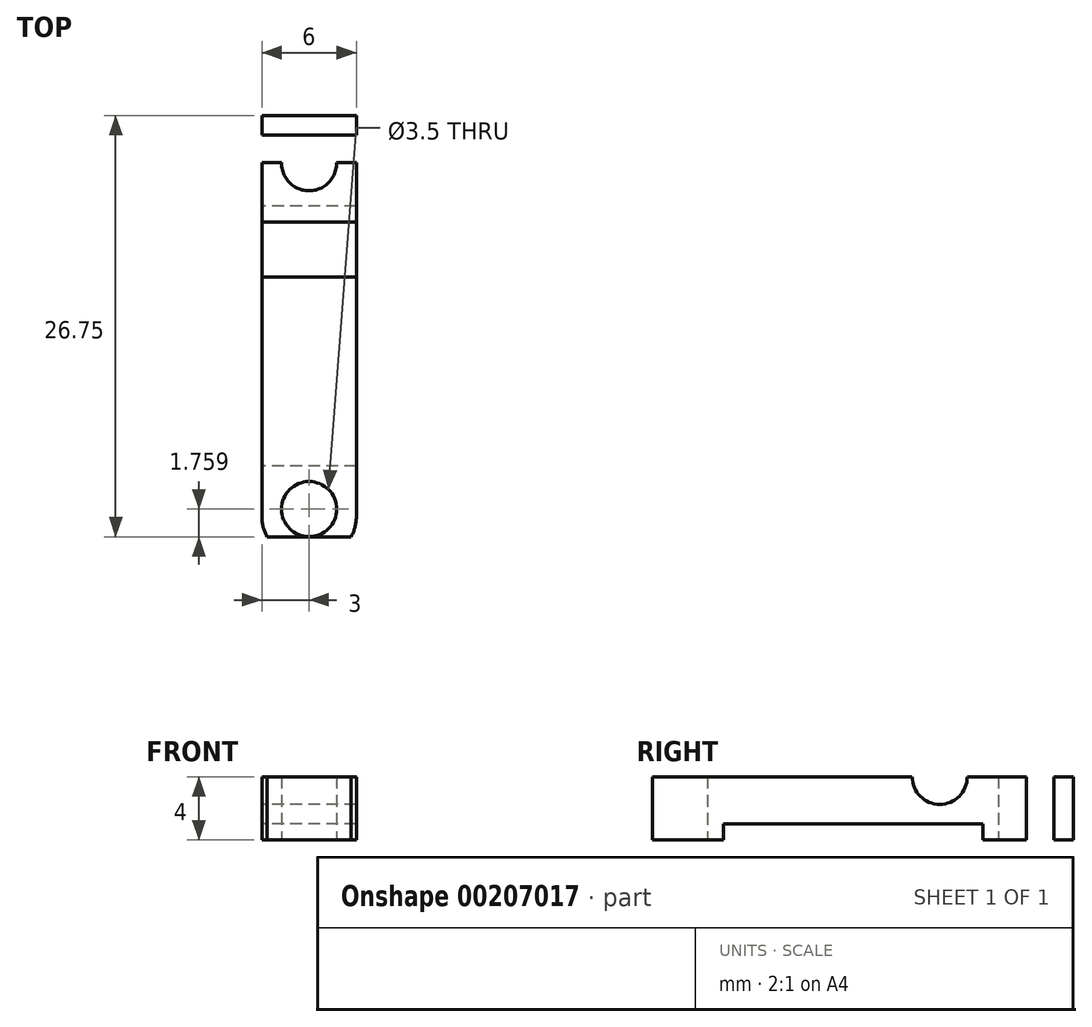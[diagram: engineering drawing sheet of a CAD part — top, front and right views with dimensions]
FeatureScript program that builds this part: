
annotation { "Feature Type Name" : "Feature", "Feature Type Description" : "" }
export const myFeature = defineFeature(function(context is Context, id is Id, definition is map)
    precondition{}
    {
        {
            var Q0;
            Q0=qCreatedBy(makeId("Right.planeOp"),FACE);
            var sketch = newSketch(context, id + "F0", { "sketchPlane" : qUnion([Q0])});
            skLineSegment(sketch, "E0.bottom", {"start": v(-33.45, -2.24) * mm, "end": v(-38.2, -2.24) * mm});
            skLineSegment(sketch, "E0.top", {"start": v(-33.45, 1.76) * mm, "end": v(-41.95, 1.76) * mm});
            skLineSegment(sketch, "E0.left", {"start": v(-33.45, -2.24) * mm, "end": v(-33.45, 1.76) * mm});
            skLineSegment(sketch, "E0.right", {"start": v(-61.45, -2.24) * mm, "end": v(-61.45, 1.76) * mm});
            skPoint(sketch, "E0.middle", {"position": v(-47.45, -0.24) * mm});
            skLineSegment(sketch, "E1", {"start": v(-61.45, -2.24) * mm, "end": v(-58.45, -2.24) * mm});
            skLineSegment(sketch, "E2", {"start": v(-58.45, 1.76) * mm, "end": v(-58.45, -2.24) * mm});
            skLineSegment(sketch, "E3", {"start": v(-33.45, -2.24) * mm, "end": v(-36.45, -2.24) * mm});
            skLineSegment(sketch, "E4", {"start": v(-36.45, -2.24) * mm, "end": v(-36.45, 1.76) * mm});
            skLineSegment(sketch, "E5", {"start": v(-61.45, 1.76) * mm, "end": v(-42.45, 1.76) * mm});
            skLineSegment(sketch, "E6", {"start": v(-33.45, 1.76) * mm, "end": v(-41.45, 1.76) * mm});
            skCircle(sketch, "E7", {"center": v(-41.95, 1.76) * mm, "radius": 1.75 * mm});
            skLineSegment(sketch, "E8", {"start": v(-36.45, 1.76) * mm, "end": v(-38.2, 1.76) * mm});
            skLineSegment(sketch, "E9", {"start": v(-38.2, 1.76) * mm, "end": v(-34.7, 1.76) * mm});
            skLineSegment(sketch, "E10", {"start": v(-58.45, 1.76) * mm, "end": v(-56.7, 1.76) * mm});
            skLineSegment(sketch, "E11", {"start": v(-56.7, 1.76) * mm, "end": v(-60.2, 1.76) * mm});
            skLineSegment(sketch, "E12", {"start": v(-60.2, 1.76) * mm, "end": v(-61.45, 1.76) * mm});
            skLineSegment(sketch, "E13", {"start": v(-58.45, -2.24) * mm, "end": v(-56.7, -2.24) * mm});
            skLineSegment(sketch, "E14", {"start": v(-56.7, 1.76) * mm, "end": v(-56.7, -2.24) * mm});
            skLineSegment(sketch, "E15", {"start": v(-56.7, -2.24) * mm, "end": v(-56.7, -1.49) * mm});
            skPoint(sketch, "E16.visualSharp", {"position": v(-56.7, -1.24) * mm});
            skPoint(sketch, "E17.visualSharp", {"position": v(-38.2, -1.24) * mm});
            skLineSegment(sketch, "E18", {"start": v(-61.45, -0.24) * mm, "end": v(-61.45, 1.76) * mm});
            skLineSegment(sketch, "E19", {"start": v(-61.45, -0.24) * mm, "end": v(-61.45, -2.24) * mm});
            skLineSegment(sketch, "E20", {"start": v(-60.2, 1.76) * mm, "end": v(-60.2, -2.24) * mm});
            skLineSegment(sketch, "E21.trimOffspring", {"start": v(-38.2, -2.24) * mm, "end": v(-36.45, -2.24) * mm});
            skLineSegment(sketch, "E22.trimOffspring", {"start": v(-56.7, -2.24) * mm, "end": v(-61.45, -2.24) * mm});
            skLineSegment(sketch, "E23.trimOffspring", {"start": v(-42.45, 1.76) * mm, "end": v(-61.45, 1.76) * mm});
            skLineSegment(sketch, "E24", {"start": v(-34.7, 1.76) * mm, "end": v(-34.7, -2.24) * mm});
            skLineSegment(sketch, "E25", {"start": v(-34.7, -2.24) * mm, "end": v(-33.45, -2.24) * mm});
            skLineSegment(sketch, "E26", {"start": v(-56.7, -2.24) * mm, "end": v(-55.7, -2.24) * mm});
            skLineSegment(sketch, "E27", {"start": v(-55.7, -1.24) * mm, "end": v(-55.7, -2.24) * mm});
            skLineSegment(sketch, "E28", {"start": v(-38.2, -2.24) * mm, "end": v(-39.2, -2.24) * mm});
            skLineSegment(sketch, "E29", {"start": v(-39.2, -1.24) * mm, "end": v(-39.2, -2.24) * mm});
            skLineSegment(sketch, "E30", {"start": v(-55.7, -1.24) * mm, "end": v(-39.2, -1.24) * mm});
            skCircle(sketch, "E31", {"center": v(-41.95, 1.76) * mm, "radius": 0.75 * mm});
            skSolve(sketch);
        }
        {
            var Q0;
            {var subQ0=sQuery(id+"F0.wireOp",EDGE,"E2");Q0=makeQuery(id+"F0.imprint","IMPRINT",FACE,{"disambiguationData":[TD([[makeQuery(id+"F0.imprint","IMPRINT",EDGE,{"derivedFrom":subQ0}),-1.0]])]});}
            var Q1;
            {var subQ3=sQuery(id+"F0.wireOp",EDGE,"E18");Q1=makeQuery(id+"F0.imprint","IMPRINT",FACE,{"disambiguationData":[TD([[makeQuery(id+"F0.imprint","IMPRINT",EDGE,{"derivedFrom":subQ3}),-1.0]])]});}
            var Q2;
            {var subQ1=sQuery(id+"F0.wireOp",EDGE,"E2");Q2=makeQuery(id+"F0.imprint","IMPRINT",FACE,{"disambiguationData":[TD([[makeQuery(id+"F0.imprint","IMPRINT",EDGE,{"derivedFrom":subQ1}),1.0]])]});}
            var Q3;
            {var subQ5=sQuery(id+"F0.wireOp",EDGE,"E4");Q3=makeQuery(id+"F0.imprint","IMPRINT",FACE,{"disambiguationData":[TD([[makeQuery(id+"F0.imprint","IMPRINT",EDGE,{"derivedFrom":subQ5}),1.0]])]});}
            var Q4;
            Q4=makeQuery(id+"F0.imprint","IMPRINT",FACE,{"disambiguationData":[TD([[makeQuery(id+"F0.imprint","IMPRINT",EDGE,{"derivedFrom":sQuery(id+"F0.wireOp",EDGE,"E3")}),-1.0]])]});
            var Q5;
            {var subQ0=sQuery(id+"F0.wireOp",EDGE,"E0.left");Q5=makeQuery(id+"F0.imprint","IMPRINT",FACE,{"disambiguationData":[TD([[makeQuery(id+"F0.imprint","IMPRINT",EDGE,{"derivedFrom":subQ0}),1.0]])]});}
            var Q6;
            {var subQ0=sQuery(id+"F0.wireOp",EDGE,"WMJeREet-rv2W-o0bE-LlzW-7S0Tiu1yK52V");var subQ1=sQuery(id+"F0.wireOp",EDGE,"E6");var subQ2=makeQuery(id+"F0.imprint","INTERSECT",VERTEX,{"derivedFrom":[subQ1,subQ0]});Q6=makeQuery(id+"F0.imprint","IMPRINT",FACE,{"disambiguationData":[TD([[makeQuery(id+"F0.imprint","IMPRINT",EDGE,{"disambiguationData":[TD([[subQ2,1.0]])],"derivedFrom":subQ1}),1.0]])]});}
            var Q7;
            {var subQ0=sQuery(id+"F0.wireOp",EDGE,"WMJeREet-rv2W-o0bE-LlzW-7S0Tiu1yK52V");var subQ1=sQuery(id+"F0.wireOp",EDGE,"E6");var subQ2=makeQuery(id+"F0.imprint","INTERSECT",VERTEX,{"derivedFrom":[subQ1,subQ0]});Q7=makeQuery(id+"F0.imprint","IMPRINT",FACE,{"disambiguationData":[TD([[makeQuery(id+"F0.imprint","IMPRINT",EDGE,{"disambiguationData":[TD([[subQ2,1.0]])],"derivedFrom":subQ1}),-1.0]])]});}
            extrude(context, id + "F1", {"entities" : qUnion([Q0, Q1, Q2, Q3, Q4, Q5, Q6, Q7]), "depth" : 6 * mm});
        }
        {
            var Q0;
            Q0=makeQuery(id+"F1.opExtrude","SWEPT_FACE",FACE,{"disambiguationData":[OSD([sQuery(id+"F0.wireOp",EDGE,"E22.trimOffspring"),sQuery(id+"F0.wireOp",EDGE,"E26")])]});
            var sketch = newSketch(context, id + "F2", { "sketchPlane" : qUnion([Q0])});
            skLineSegment(sketch, "E32", {"start": v(0, 58.44) * mm, "end": v(6, 58.44) * mm});
            skCircle(sketch, "E33", {"center": v(3, 58.44) * mm, "radius": 1.75 * mm});
            skLineSegment(sketch, "E34", {"start": v(0, 58.44) * mm, "end": v(0, 58.95) * mm});
            skLineSegment(sketch, "E35", {"start": v(2.5, 61.45) * mm, "end": v(3.5, 61.45) * mm});
            skLineSegment(sketch, "E36", {"start": v(6, 58.95) * mm, "end": v(6, 58.44) * mm});
            skPoint(sketch, "E37.visualSharp", {"position": v(0, 61.45) * mm});
            skArc(sketch, "E37.filletArc", {"start": v(2.5, 61.45) * mm, "mid": v(0.73, 60.71) * mm, "end": v(0, 58.95) * mm});
            skPoint(sketch, "E38.visualSharp", {"position": v(6, 61.45) * mm});
            skArc(sketch, "E38.filletArc", {"start": v(6, 58.95) * mm, "mid": v(5.27, 60.71) * mm, "end": v(3.5, 61.45) * mm});
            skSolve(sketch);
        }
        {
            var Q0;
            Q0=makeQuery(id+"F1.opExtrude","SWEPT_FACE",FACE,{"disambiguationData":[OSD([sQuery(id+"F0.wireOp",EDGE,"E3"),sQuery(id+"F0.wireOp",EDGE,"E21.trimOffspring"),sQuery(id+"F0.wireOp",EDGE,"E25"),sQuery(id+"F0.wireOp",EDGE,"E28")])]});
            var sketch = newSketch(context, id + "F3", { "sketchPlane" : qUnion([Q0])});
            skLineSegment(sketch, "E39", {"start": v(0, 36.47) * mm, "end": v(6, 36.47) * mm});
            skCircle(sketch, "E40", {"center": v(3, 36.47) * mm, "radius": 1.75 * mm});
            skLineSegment(sketch, "E41", {"start": v(0, 36.47) * mm, "end": v(0, 35.95) * mm});
            skLineSegment(sketch, "E42", {"start": v(2.5, 33.45) * mm, "end": v(3.5, 33.45) * mm});
            skLineSegment(sketch, "E43", {"start": v(6, 35.95) * mm, "end": v(6, 36.47) * mm});
            skPoint(sketch, "E44.visualSharp", {"position": v(0, 33.45) * mm});
            skArc(sketch, "E44.filletArc", {"start": v(0, 35.95) * mm, "mid": v(0.73, 34.18) * mm, "end": v(2.5, 33.45) * mm});
            skPoint(sketch, "E45.visualSharp", {"position": v(6, 33.45) * mm});
            skArc(sketch, "E45.filletArc", {"start": v(3.5, 33.45) * mm, "mid": v(5.27, 34.18) * mm, "end": v(6, 35.95) * mm});
            skSolve(sketch);
        }
        {
            var Q0;
            {var subQ0=sQuery(id+"F2.wireOp",EDGE,"E37.filletArc");Q0=makeQuery(id+"F2.imprint","IMPRINT",FACE,{"disambiguationData":[TD([[makeQuery(id+"F2.imprint","IMPRINT",EDGE,{"derivedFrom":subQ0}),-1.0]])]});}
            var Q1;
            {var subQ0=sQuery(id+"F2.wireOp",EDGE,"E38.filletArc");Q1=makeQuery(id+"F2.imprint","IMPRINT",FACE,{"disambiguationData":[TD([[makeQuery(id+"F2.imprint","IMPRINT",EDGE,{"derivedFrom":subQ0}),-1.0]])]});}
            extrude(context, id + "F4", {"entities" : qUnion([Q0, Q1]), "operationType" : NewBodyOperationType.REMOVE, "oppositeDirection" : true, "depth" : 4 * mm});
        }
        {
            var Q0;
            {var subQ0=sQuery(id+"F2.wireOp",EDGE,"E33");var subQ1=sQuery(id+"F2.wireOp",EDGE,"E32");var subQ2=makeQuery(id+"F2.imprint","INTERSECT",VERTEX,{"disambiguationData":[OD(0.0)],"derivedFrom":[subQ1,subQ0]});Q0=makeQuery(id+"F2.imprint","IMPRINT",FACE,{"disambiguationData":[TD([[makeQuery(id+"F2.imprint","IMPRINT",EDGE,{"disambiguationData":[TD([[subQ2,-1.0]])],"derivedFrom":subQ1}),1.0]])]});}
            var Q1;
            {var subQ0=sQuery(id+"F2.wireOp",EDGE,"E33");var subQ1=sQuery(id+"F2.wireOp",EDGE,"E32");var subQ2=makeQuery(id+"F2.imprint","INTERSECT",VERTEX,{"disambiguationData":[OD(0.0)],"derivedFrom":[subQ1,subQ0]});Q1=makeQuery(id+"F2.imprint","IMPRINT",FACE,{"disambiguationData":[TD([[makeQuery(id+"F2.imprint","IMPRINT",EDGE,{"disambiguationData":[TD([[subQ2,-1.0]])],"derivedFrom":subQ1}),-1.0]])]});}
            extrude(context, id + "F5", {"entities" : qUnion([Q0, Q1]), "operationType" : NewBodyOperationType.REMOVE, "oppositeDirection" : true, "depth" : 4 * mm});
        }
        {
            var Q0;
            {var subQ0=sQuery(id+"F3.wireOp",EDGE,"E40");var subQ1=sQuery(id+"F3.wireOp",EDGE,"E39");var subQ2=makeQuery(id+"F3.imprint","INTERSECT",VERTEX,{"disambiguationData":[OD(0.0)],"derivedFrom":[subQ1,subQ0]});Q0=makeQuery(id+"F3.imprint","IMPRINT",FACE,{"disambiguationData":[TD([[makeQuery(id+"F3.imprint","IMPRINT",EDGE,{"disambiguationData":[TD([[subQ2,-1.0]])],"derivedFrom":subQ1}),1.0]])]});}
            var Q1;
            {var subQ0=sQuery(id+"F3.wireOp",EDGE,"E45.filletArc");Q1=makeQuery(id+"F3.imprint","IMPRINT",FACE,{"disambiguationData":[TD([[makeQuery(id+"F3.imprint","IMPRINT",EDGE,{"derivedFrom":subQ0}),-1.0]])]});}
            var Q2;
            {var subQ0=sQuery(id+"F3.wireOp",EDGE,"E44.filletArc");Q2=makeQuery(id+"F3.imprint","IMPRINT",FACE,{"disambiguationData":[TD([[makeQuery(id+"F3.imprint","IMPRINT",EDGE,{"derivedFrom":subQ0}),-1.0]])]});}
            var Q3;
            {var subQ0=sQuery(id+"F3.wireOp",EDGE,"E40");var subQ1=sQuery(id+"F3.wireOp",EDGE,"E39");var subQ2=makeQuery(id+"F3.imprint","INTERSECT",VERTEX,{"disambiguationData":[OD(0.0)],"derivedFrom":[subQ1,subQ0]});Q3=makeQuery(id+"F3.imprint","IMPRINT",FACE,{"disambiguationData":[TD([[makeQuery(id+"F3.imprint","IMPRINT",EDGE,{"disambiguationData":[TD([[subQ2,-1.0]])],"derivedFrom":subQ1}),-1.0]])]});}
            extrude(context, id + "F6", {"entities" : qUnion([Q0, Q1, Q2, Q3]), "operationType" : NewBodyOperationType.REMOVE, "oppositeDirection" : true, "depth" : 4 * mm});
        }
    });
